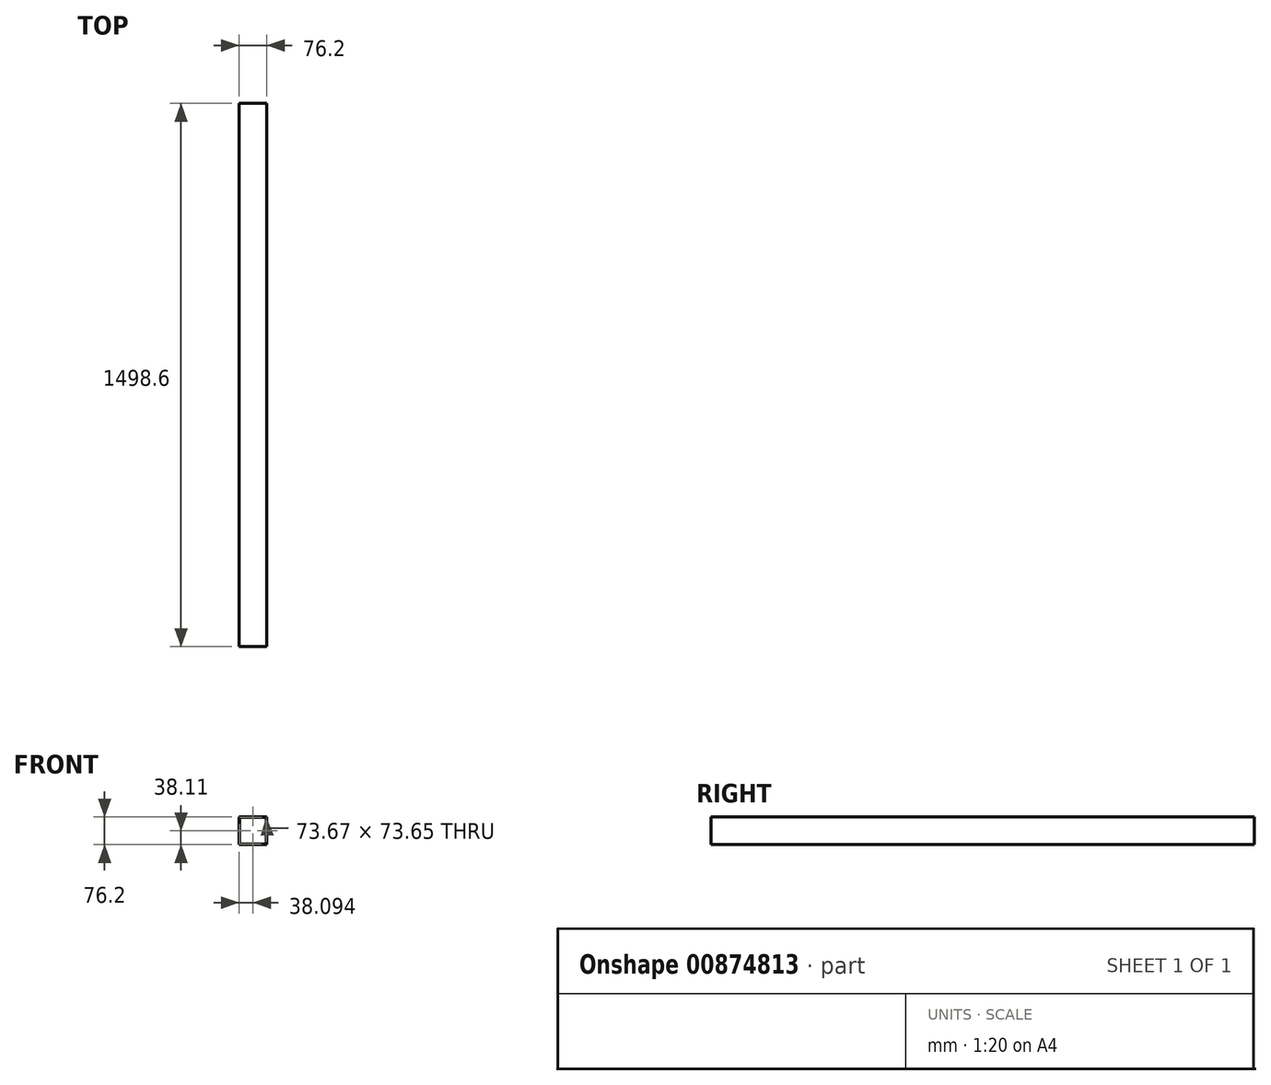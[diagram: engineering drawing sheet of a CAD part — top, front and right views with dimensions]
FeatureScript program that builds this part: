
annotation { "Feature Type Name" : "Feature", "Feature Type Description" : "" }
export const myFeature = defineFeature(function(context is Context, id is Id, definition is map)
    precondition{}
    {
        {
            var Q0;
            Q0=qCreatedBy(makeId("Front.planeOp"),FACE);
            var sketch = newSketch(context, id + "F0", { "sketchPlane" : qUnion([Q0])});
            skLineSegment(sketch, "E0.bottom", {"start": v(-117.25, 89.57) * mm, "end": v(-41.05, 89.57) * mm});
            skLineSegment(sketch, "E0.top", {"start": v(-117.25, 13.37) * mm, "end": v(-41.05, 13.37) * mm});
            skLineSegment(sketch, "E0.left", {"start": v(-117.25, 89.57) * mm, "end": v(-117.25, 13.37) * mm});
            skLineSegment(sketch, "E0.right", {"start": v(-41.05, 89.57) * mm, "end": v(-41.05, 13.37) * mm});
            skSolve(sketch);
        }
        {
            var Q0;
            Q0=qSketchRegion(id+"F0",true);
            extrude(context, id + "F1", {"entities" : qUnion([Q0]), "depth" : 609.6 * mm, "offsetDistance" : 25.4 * mm});
        }
        {
            var Q0;
            Q0=makeQuery(id+"F1.opExtrude","CAP_FACE",FACE,{"disambiguationData":[OSD([sQuery(id+"F0.wireOp",EDGE,"E0.bottom"),sQuery(id+"F0.wireOp",EDGE,"E0.top"),sQuery(id+"F0.wireOp",EDGE,"E0.left"),sQuery(id+"F0.wireOp",EDGE,"E0.right")])],"isStart":false});
            var sketch = newSketch(context, id + "F2", { "sketchPlane" : qUnion([Q0])});
            skLineSegment(sketch, "E1", {"start": v(-98.69, 89.57) * mm, "end": v(-98.69, 88.3) * mm});
            skLineSegment(sketch, "E2", {"start": v(-98.69, 88.3) * mm, "end": v(-116, 88.3) * mm});
            skLineSegment(sketch, "E3", {"start": v(-116, 88.3) * mm, "end": v(-116, 14.66) * mm});
            skLineSegment(sketch, "E4", {"start": v(-116, 14.66) * mm, "end": v(-42.32, 14.66) * mm});
            skLineSegment(sketch, "E5", {"start": v(-42.32, 14.66) * mm, "end": v(-42.32, 88.3) * mm});
            skLineSegment(sketch, "E6", {"start": v(-42.32, 88.3) * mm, "end": v(-98.69, 88.3) * mm});
            skSolve(sketch);
        }
        {
            var Q0;
            Q0=makeQuery(id+"F2.imprint","IMPRINT",FACE,{"disambiguationData":[TD([[makeQuery(id+"F2.imprint","IMPRINT",EDGE,{"derivedFrom":sQuery(id+"F2.wireOp",EDGE,"E2")}),1.0]])]});
            extrude(context, id + "F3", {"entities" : qUnion([Q0]), "operationType" : NewBodyOperationType.REMOVE, "oppositeDirection" : true, "depth" : 914.4 * mm, "offsetDistance" : 25.4 * mm});
        }
        {
            var Q0;
            Q0=makeQuery(id+"F1.opExtrude","CAP_FACE",FACE,{"disambiguationData":[OSD([sQuery(id+"F0.wireOp",EDGE,"E0.bottom"),sQuery(id+"F0.wireOp",EDGE,"E0.top"),sQuery(id+"F0.wireOp",EDGE,"E0.left"),sQuery(id+"F0.wireOp",EDGE,"E0.right")])],"isStart":false});
            extrude(context, id + "F4", {"entities" : qUnion([Q0]), "operationType" : NewBodyOperationType.ADD, "depth" : 304.8 * mm, "offsetDistance" : 25.4 * mm});
        }
        {
            var Q0;
            Q0=makeQuery(id+"F1.opExtrude","CAP_FACE",FACE,{"disambiguationData":[OSD([sQuery(id+"F0.wireOp",EDGE,"E0.bottom"),sQuery(id+"F0.wireOp",EDGE,"E0.top"),sQuery(id+"F0.wireOp",EDGE,"E0.left"),sQuery(id+"F0.wireOp",EDGE,"E0.right")])],"isStart":true});
            extrude(context, id + "F5", {"entities" : qUnion([Q0]), "operationType" : NewBodyOperationType.ADD, "depth" : 584.2 * mm, "offsetDistance" : 25.4 * mm});
        }
    });
